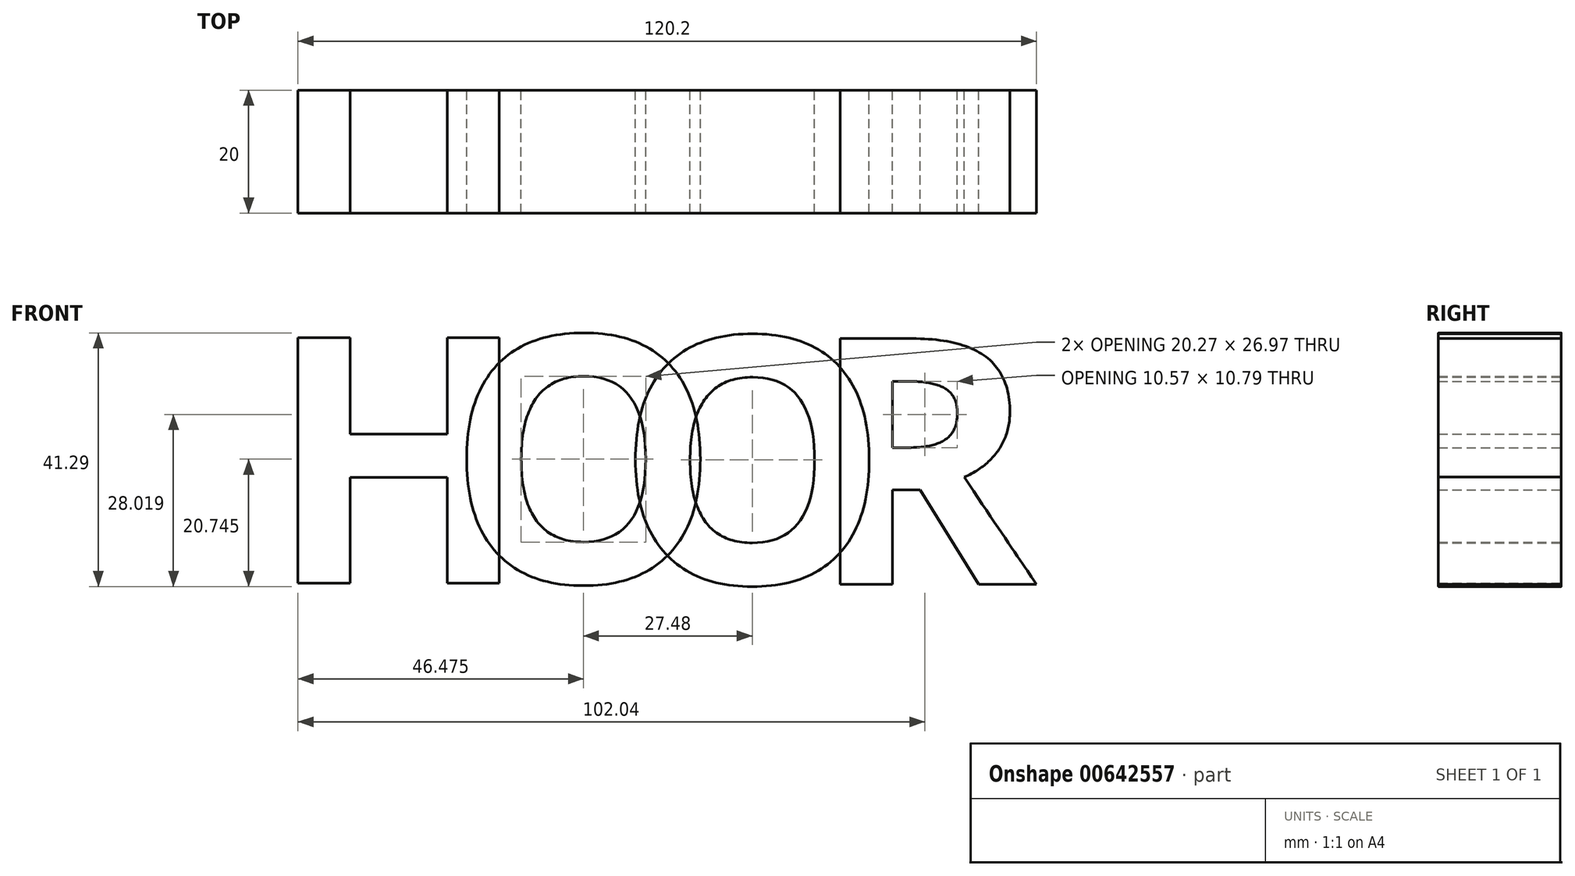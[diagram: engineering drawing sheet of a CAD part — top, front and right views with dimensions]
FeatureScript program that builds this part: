
annotation { "Feature Type Name" : "Feature", "Feature Type Description" : "" }
export const myFeature = defineFeature(function(context is Context, id is Id, definition is map)
    precondition{}
    {
        {
            var Q0;
            Q0=qCreatedBy(makeId("Front.planeOp"),FACE);
            var sketch = newSketch(context, id + "F0", { "sketchPlane" : qUnion([Q0])});
            skText(sketch, "E0", { "text": "H", "fontName": "OpenSans-Bold.ttf"});
            const initialGuessF0  = {"E0": [-0.06918, -0.01095, 1, 0, 0.0403]};
            skSetInitialGuess(sketch, initialGuessF0);
            skSolve(sketch);
        }
        {
            var Q0;
            Q0=makeQuery(id+"F0.imprint","IMPRINT",FACE,{"disambiguationData":[TD([[makeQuery(id+"F0.imprint","IMPRINT",EDGE,{"derivedFrom":sQuery(id+"F0.wireOp",EDGE,"E0.sketch_text.stroke-0")}),-1.0]])]});
            var sketch = newSketch(context, id + "F1", { "sketchPlane" : qUnion([Q0])});
            skText(sketch, "E1", { "text": "O", "fontName": "OpenSans-Bold.ttf"});
            const initialGuessF1  = {"E1": [-0.03995, -0.0108, 1, 0, 0.0403]};
            skSetInitialGuess(sketch, initialGuessF1);
            skSolve(sketch);
        }
        {
            var Q0;
            Q0=qCreatedBy(makeId("Front.planeOp"),FACE);
            var sketch = newSketch(context, id + "F2", { "sketchPlane" : qUnion([Q0])});
            skText(sketch, "E2", { "text": "O", "fontName": "OpenSans-Bold.ttf"});
            const initialGuessF2  = {"E2": [-0.01247, -0.01095, 1, 0, 0.0403]};
            skSetInitialGuess(sketch, initialGuessF2);
            skSolve(sketch);
        }
        {
            var Q0;
            Q0=qCreatedBy(makeId("Front.planeOp"),FACE);
            var sketch = newSketch(context, id + "F3", { "sketchPlane" : qUnion([Q0])});
            skText(sketch, "E3", { "text": "R", "fontName": "OpenSans-Bold.ttf"});
            const initialGuessF3  = {"E3": [0.0191, -0.0111, 1, 0, 0.0403]};
            skSetInitialGuess(sketch, initialGuessF3);
            skSolve(sketch);
        }
        {
            var Q0;
            Q0 = qSketchRegion(id + "F1", true);
            var Q1;
            Q1 = qSketchRegion(id + "F2", true);
            var Q2;
            Q2 = qSketchRegion(id + "F0", true);
            var Q3;
            Q3 = qSketchRegion(id + "F3", true);
            extrude(context, id + "F4", {"entities" : qUnion([Q0, Q1, Q2, Q3]), "depth" : 20 * mm, "offsetDistance" : 25 * mm});
        }
    });
